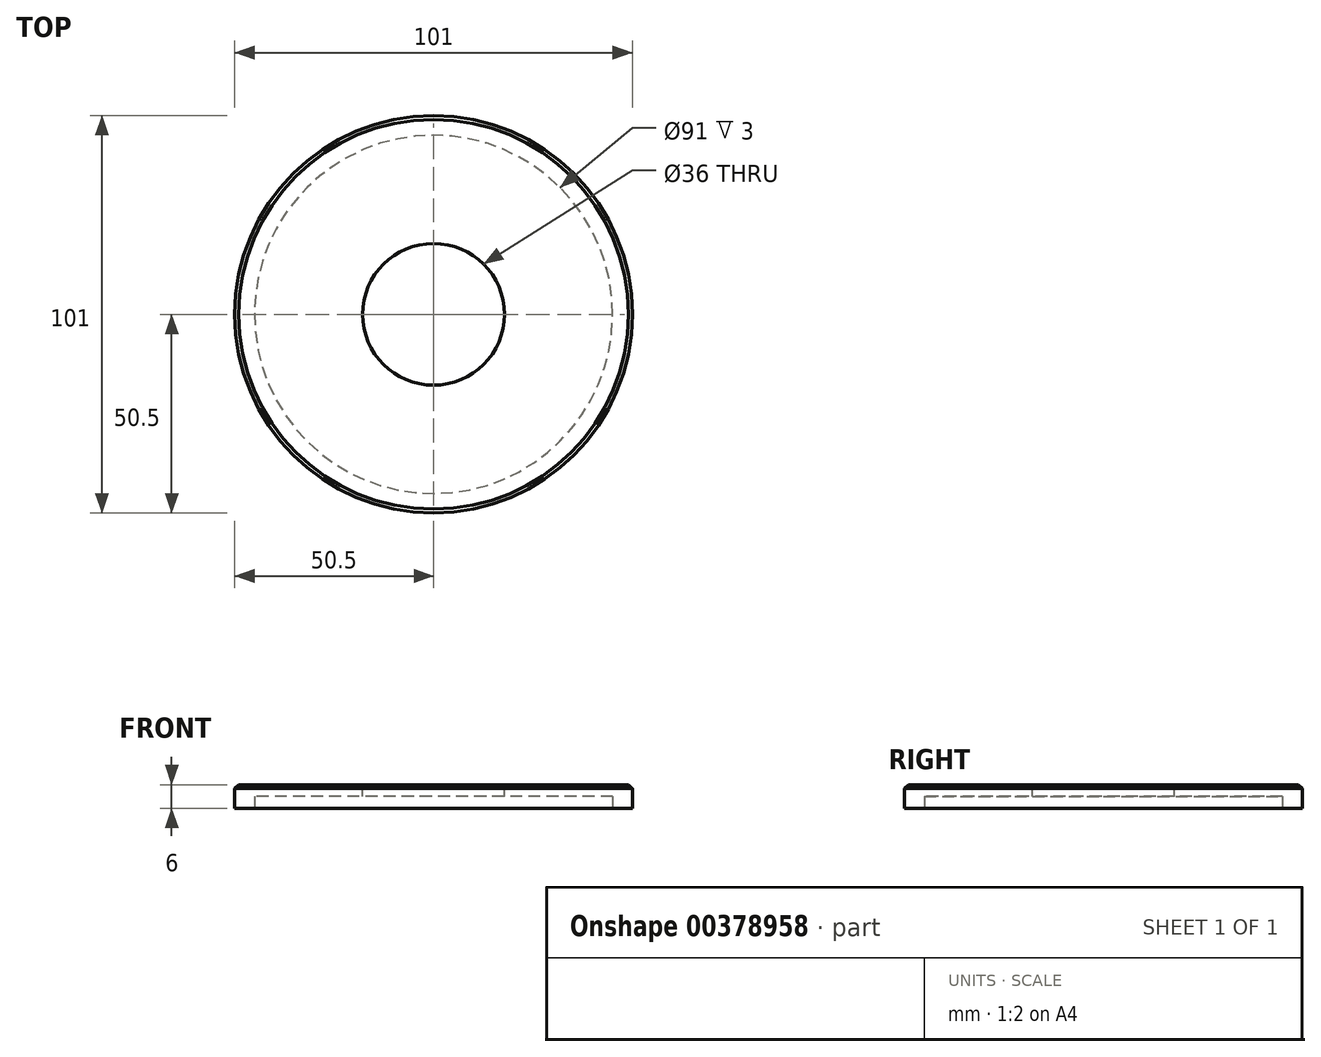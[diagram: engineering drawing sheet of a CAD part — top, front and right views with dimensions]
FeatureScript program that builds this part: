
annotation { "Feature Type Name" : "Feature", "Feature Type Description" : "" }
export const myFeature = defineFeature(function(context is Context, id is Id, definition is map)
    precondition{}
    {
        {
            var Q0;
            Q0=qCreatedBy(makeId("Top.planeOp"),FACE);
            var sketch = newSketch(context, id + "F0", { "sketchPlane" : qUnion([Q0])});
            skCircle(sketch, "E0", {"center": v(0, 0) * mm, "radius": 45 * mm, "construction": true});
            skCircle(sketch, "E1", {"center": v(0, 0) * mm, "radius": 45.5 * mm});
            skCircle(sketch, "E2.0", {"center": v(0, 0) * mm, "radius": 50.5 * mm});
            skSolve(sketch);
        }
        {
            var Q0;
            Q0=makeQuery(id+"F0.imprint","IMPRINT",FACE,{"disambiguationData":[TD([[makeQuery(id+"F0.imprint","IMPRINT",EDGE,{"derivedFrom":sQuery(id+"F0.wireOp",EDGE,"E1")}),1.0]])]});
            var Q1;
            Q1=makeQuery(id+"F0.imprint","IMPRINT",FACE,{"disambiguationData":[TD([[makeQuery(id+"F0.imprint","IMPRINT",EDGE,{"derivedFrom":sQuery(id+"F0.wireOp",EDGE,"E1")}),-1.0]])]});
            extrude(context, id + "F1", {"entities" : qUnion([Q0, Q1]), "depth" : 6 * mm});
        }
        {
            var Q0;
            Q0=makeQuery(id+"F0.imprint","IMPRINT",FACE,{"disambiguationData":[TD([[makeQuery(id+"F0.imprint","IMPRINT",EDGE,{"derivedFrom":sQuery(id+"F0.wireOp",EDGE,"E1")}),1.0]])]});
            extrude(context, id + "F2", {"entities" : qUnion([Q0]), "operationType" : NewBodyOperationType.REMOVE, "depth" : 3 * mm});
        }
        {
            var Q0;
            Q0=makeQuery(id+"F1.opExtrude","CAP_FACE",FACE,{"disambiguationData":[OSD([sQuery(id+"F0.wireOp",EDGE,"E2.0")])],"isStart":false});
            var sketch = newSketch(context, id + "F3", { "sketchPlane" : qUnion([Q0])});
            skCircle(sketch, "E3", {"center": v(0, 0) * mm, "radius": 18 * mm});
            skSolve(sketch);
        }
        {
            var Q0;
            Q0 = qSketchRegion(id + "F3", true);
            extrude(context, id + "F4", {"entities" : qUnion([Q0]), "operationType" : NewBodyOperationType.REMOVE, "endBound" : BoundingType.THROUGH_ALL, "oppositeDirection" : true, "depth" : 25 * mm});
        }
        {
            var Q0;
            Q0=makeQuery(id+"F4.boolean.opBoolean","COPY",EDGE,{"derivedFrom":makeQuery(id+"F4.opExtrude","CAP_EDGE",EDGE,{"disambiguationData":[OSD([sQuery(id+"F3.wireOp",EDGE,"E3")])],"isStart":true})});
            var Q1;
            Q1=makeQuery(id+"F1.opExtrude","CAP_EDGE",EDGE,{"disambiguationData":[OSD([sQuery(id+"F0.wireOp",EDGE,"E2.0")])],"isStart":false});
            chamfer(context, id + "F5", {"entities" : qUnion([Q0, Q1]), "width" : 1 * mm, "tangentPropagation" : true});
        }
    });
